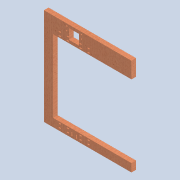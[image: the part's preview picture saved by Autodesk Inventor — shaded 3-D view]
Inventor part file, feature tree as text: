
AUTODESK INVENTOR PART (.ipt)
format: ipt  version: 2020 (Build 240168000, 168)  size: 267,776 bytes
history: native  units: mm
features: extrude x5, sketch x4, other x3, pattern_linear x1, hole x1, reference x1
ambient origin geometry x8: Origin, YZ Plane, XZ Plane, XY Plane, X Axis, Y Axis, Z Axis, Center Point
bodies: Solid1 (feature_tree)
feature tree (15):
  extrude  "Extrusion1"  Depth=420.0mm
  extrude  "Extrusion5"  Depth=70.0mm
  extrude  "Extrusion6"  Depth=40.0mm
  extrude  "Extrusion8"  Depth=10.0mm
  extrude  "Extrusion9"  Depth=10.0mm
  pattern_linear  "Rectangular Pattern1"  Spacing1=4.5mm  [1 undecoded]
  hole  "Hole1"  [1 undecoded]
  sketch  "Sketch1"  dims[d0=380.0mm d1=420.0mm]
  sketch  "Sketch6"  dims[d2=20.0mm d3=0.0mm d24=70.0mm]
  sketch  "Sketch9"  dims[d25=35.0mm d26=40.0mm]
  reference  "Reference13"
  sketch  "Sketch10"  dims[d27=0.0mm d28=0.0mm d30=15.0mm d32=121.194mm d33=4.5mm d34=10.0mm d36=20.0mm d37=0.0mm d38=0.0mm d43=0.0mm d44=0.0mm d45=44.0mm d50=35.0mm d51=16.0mm d52=5.0mm d53=4.5mm d54=68.694mm d55=47.0mm d56=68.7mm d59=0.0mm d60=0.0mm d61=20.0mm d63=90.0mm d64=20.0mm d66=345.0mm d67=130.694mm d68=7.0mm d69=64.0mm d70=10.0mm d71=17.0mm d72=5.0mm d73=6.0mm d74=4.0mm d75=2.0mm d76=90.0deg d77=8.0mm d78=20.594885mm]
  parser-record x1  (decoder bookkeeping rows leaked as tree rows — omitted from the tree; the rows remain in map.json)
  other  "0005-00-00 Ansamblu_General.iam"
  other  "0005-10-015 suport tija.ipt:51"
note: 2 required parameter values undecoded (feature->parameter linkage not recoverable at this tier; creation-order binding heuristic only, values carry confidence <= 0.55)
note: 1 file-system path scrubbed to <path> (originals preserved in map.json)
